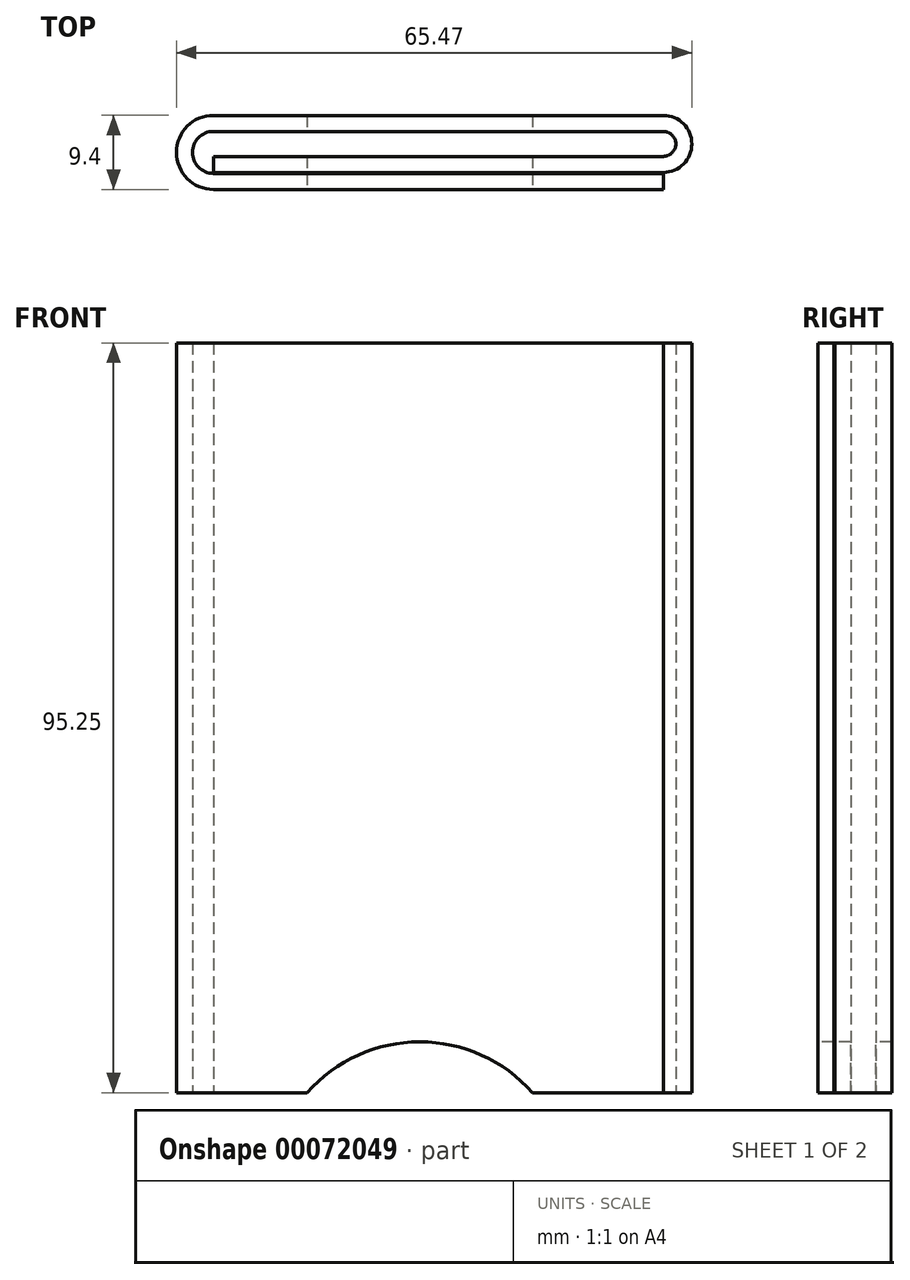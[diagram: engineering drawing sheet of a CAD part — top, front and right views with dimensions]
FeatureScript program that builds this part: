
annotation { "Feature Type Name" : "Feature", "Feature Type Description" : "" }
export const myFeature = defineFeature(function(context is Context, id is Id, definition is map)
    precondition{}
    {
        {
            var Q0;
            Q0=qCreatedBy(makeId("Top.planeOp"),FACE);
            var sketch = newSketch(context, id + "F3", { "sketchPlane" : qUnion([Q0])});
            skLineSegment(sketch, "E0", {"start": v(0, 4.7) * mm, "end": v(57.15, 4.7) * mm});
            skArc(sketch, "E1", {"start": v(0, 4.7) * mm, "mid": v(-4.7, 0) * mm, "end": v(0, -4.7) * mm});
            skArc(sketch, "E2", {"start": v(57.15, 4.7) * mm, "mid": v(60.77, 1.08) * mm, "end": v(57.15, -2.54) * mm});
            skLineSegment(sketch, "E3", {"start": v(57.15, -2.54) * mm, "end": v(0, -2.54) * mm});
            skLineSegment(sketch, "E4", {"start": v(0, -4.7) * mm, "end": v(57.15, -4.7) * mm});
            skLineSegment(sketch, "E5", {"start": v(57.15, -4.7) * mm, "end": v(57.15, -4.7) * mm});
            skLineSegment(sketch, "E6", {"start": v(57.15, -4.7) * mm, "end": v(57.15, -2.67) * mm});
            skLineSegment(sketch, "E7", {"start": v(57.15, -2.67) * mm, "end": v(57.15, -2.67) * mm});
            skLineSegment(sketch, "E8", {"start": v(0, -2.67) * mm, "end": v(57.15, -2.67) * mm});
            skArc(sketch, "E9", {"start": v(0, -2.67) * mm, "mid": v(-2.67, 0) * mm, "end": v(0, 2.67) * mm});
            skLineSegment(sketch, "E10", {"start": v(0, 2.67) * mm, "end": v(57.15, 2.67) * mm});
            skLineSegment(sketch, "E11", {"start": v(0, -2.54) * mm, "end": v(0, -0.5) * mm});
            skLineSegment(sketch, "E12", {"start": v(0, -0.5) * mm, "end": v(0, -0.5) * mm});
            skLineSegment(sketch, "E13", {"start": v(0, -0.5) * mm, "end": v(57.15, -0.5) * mm});
            skArc(sketch, "E14", {"start": v(57.15, -0.5) * mm, "mid": v(58.74, 1.08) * mm, "end": v(57.15, 2.67) * mm});
            skSolve(sketch);
        }
        {
            var Q0;
            Q0=makeQuery(id+"F3.imprint","IMPRINT",FACE,{"disambiguationData":[TD([[makeQuery(id+"F3.imprint","IMPRINT",EDGE,{"derivedFrom":sQuery(id+"F3.wireOp",EDGE,"E0")}),-1.0]])]});
            extrude(context, id + "F0", {"entities" : qUnion([Q0]), "depth" : 95.25 * mm});
        }
        {
            var Q0;
            Q0=qCreatedBy(makeId("Front.planeOp"),FACE);
            var sketch = newSketch(context, id + "F1", { "sketchPlane" : qUnion([Q0])});
            skCircle(sketch, "E15", {"center": v(26.21, -12.6) * mm, "radius": 19.05 * mm});
            skLineSegment(sketch, "E16", {"start": v(68.27, 0) * mm, "end": v(-4.8, 0) * mm, "construction": true});
            skSolve(sketch);
        }
        {
            var Q0;
            Q0=makeQuery(id+"F1.imprint","IMPRINT",FACE,{"disambiguationData":[TD([[makeQuery(id+"F1.imprint","IMPRINT",EDGE,{"derivedFrom":sQuery(id+"F1.wireOp",EDGE,"E15")}),1.0]])]});
            extrude(context, id + "F2", {"entities" : qUnion([Q0]), "operationType" : NewBodyOperationType.REMOVE, "endBound" : BoundingType.SYMMETRIC, "oppositeDirection" : true, "depth" : 25.4 * mm});
        }
    });
